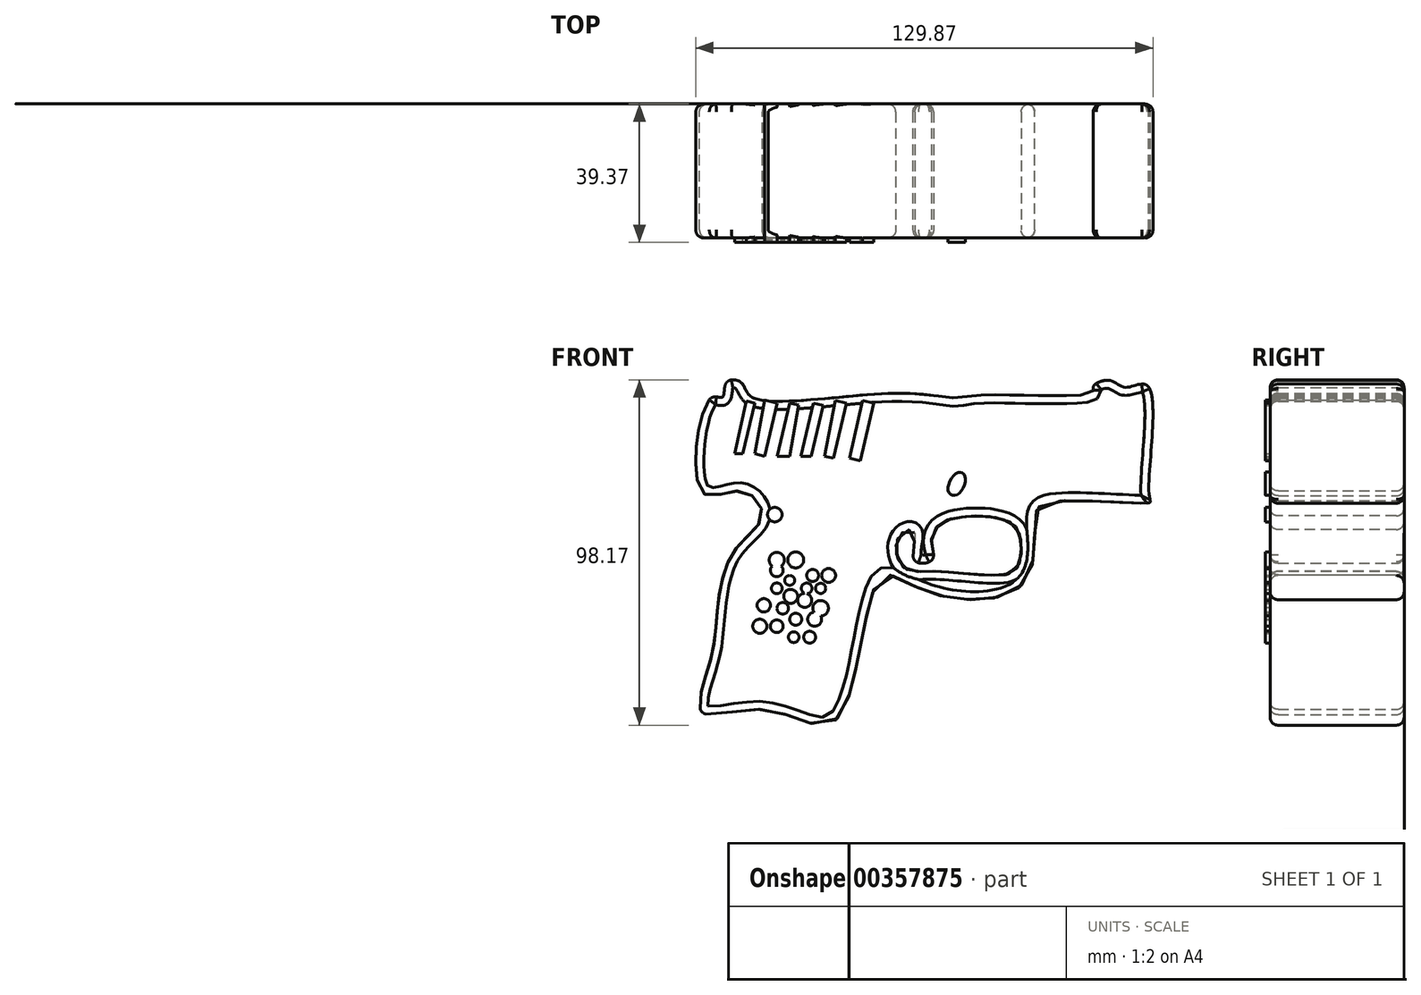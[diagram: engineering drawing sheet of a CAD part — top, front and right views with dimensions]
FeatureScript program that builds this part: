
annotation { "Feature Type Name" : "Feature", "Feature Type Description" : "" }
export const myFeature = defineFeature(function(context is Context, id is Id, definition is map)
    precondition{}
    {
        {
            var Q0;
            Q0=qCreatedBy(makeId("Front.planeOp"),FACE);
            var sketch = newSketch(context, id + "F0", { "sketchPlane" : qUnion([Q0])});
            skFitSpline(sketch, "E0", {"points": [v(-22.23, -45.44) * mm, v(-10, -5.42) * mm, v(2.22, -8.48) * mm, v(30.57, -7.09) * mm, v(34.18, 11.25) * mm, v(38.07, 16.35) * mm, v(66.7, 16.26) * mm, v(66.7, 18.2) * mm, v(66.42, 49.33) * mm, v(60.03, 49.05) * mm, v(55.58, 51) * mm, v(50.86, 49.33) * mm, v(50.58, 47.66) * mm, v(18.06, 46.83) * mm, v(11.95, 46) * mm, v(-5, 47.38) * mm, v(-46.13, 46.27) * mm, v(-49.19, 50.44) * mm, v(-53.36, 50.44) * mm, v(-54.47, 46.27) * mm, v(-57.8, 46) * mm, v(-60.3, 19.31) * mm, v(-49.19, 19.6) * mm, v(-43.2, 12.64) * mm, v(-51.13, 2.64) * mm, v(-56.14, -15.98) * mm, v(-58.08, -29.04) * mm, v(-60.33, -43.21) * mm, v(-41.96, -42.63) * mm, v(-22.23, -45.44) * mm]});
            skFitSpline(sketch, "E1", {"points": [v(-2.78, 8.2) * mm, v(-5.28, 3.75) * mm, v(-2.78, -2.36) * mm, v(4.45, -3.2) * mm, v(20.29, -4.3) * mm, v(28.9, -2.64) * mm, v(30.3, 4.86) * mm, v(27.23, 10.7) * mm, v(8.61, 10.98) * mm, v(4.9, 5.14) * mm, v(5, 0) * mm, v(0, 0) * mm, v(0, 7.92) * mm, v(-2.78, 8.2) * mm]});
            skSolve(sketch);
        }
        {
            var Q0;
            Q0=makeQuery(id+"F0.imprint","IMPRINT",FACE,{"disambiguationData":[TD([[makeQuery(id+"F0.imprint","IMPRINT",EDGE,{"derivedFrom":sQuery(id+"F0.wireOp",EDGE,"E0")}),1.0]])]});
            extrude(context, id + "F1", {"entities" : qUnion([Q0]), "depth" : 38.1 * mm});
        }
        {
            var Q0;
            Q0=makeQuery(id+"F1.opExtrude","CAP_FACE",FACE,{"disambiguationData":[OSD([sQuery(id+"F0.wireOp",EDGE,"E0"),sQuery(id+"F0.wireOp",EDGE,"E1")])],"isStart":false});
            var Q1;
            Q1=makeQuery(id+"F1.opExtrude","CAP_FACE",FACE,{"disambiguationData":[OSD([sQuery(id+"F0.wireOp",EDGE,"E0"),sQuery(id+"F0.wireOp",EDGE,"E1")])],"isStart":true});
            fillet(context, id + "F2", {"entities" : qUnion([Q0, Q1]), "radius" : 2.3 * mm, "tangentPropagation" : true, "allowEdgeOverflow" : false});
        }
        {
            var Q0;
            Q0=qCreatedBy(makeId("Front.planeOp"),FACE);
            var sketch = newSketch(context, id + "F3", { "sketchPlane" : qUnion([Q0])});
            skCircle(sketch, "E2", {"center": v(-29.74, -21.95) * mm, "radius": 1.7 * mm});
            skCircle(sketch, "E3", {"center": v(-34.27, -21.95) * mm, "radius": 1.53 * mm});
            skCircle(sketch, "E4", {"center": v(-39.08, -18.83) * mm, "radius": 1.81 * mm});
            skCircle(sketch, "E5", {"center": v(-43.9, -18.83) * mm, "radius": 2 * mm});
            skCircle(sketch, "E6", {"center": v(-42.77, -12.89) * mm, "radius": 1.9 * mm});
            skCircle(sketch, "E7", {"center": v(-28.32, -16.85) * mm, "radius": 1.98 * mm});
            skCircle(sketch, "E8", {"center": v(-33.7, -16.85) * mm, "radius": 1.7 * mm});
            skCircle(sketch, "E9", {"center": v(-37.39, -13.74) * mm, "radius": 1.65 * mm});
            skCircle(sketch, "E10", {"center": v(-39.08, -8.07) * mm, "radius": 1.53 * mm});
            skCircle(sketch, "E11", {"center": v(-35.12, -10.34) * mm, "radius": 1.98 * mm});
            skCircle(sketch, "E12", {"center": v(-31.15, -11.47) * mm, "radius": 2 * mm});
            skCircle(sketch, "E13", {"center": v(-26.62, -13.74) * mm, "radius": 2.21 * mm});
            skCircle(sketch, "E14", {"center": v(-24.36, -4.39) * mm, "radius": 1.98 * mm});
            skCircle(sketch, "E15", {"center": v(-26.62, -8.07) * mm, "radius": 1.44 * mm});
            skCircle(sketch, "E16", {"center": v(-30.59, -8.07) * mm, "radius": 1.53 * mm});
            skCircle(sketch, "E17", {"center": v(-35.4, -5.8) * mm, "radius": 1.42 * mm});
            skCircle(sketch, "E18", {"center": v(-39.08, -2.97) * mm, "radius": 1.8 * mm});
            skCircle(sketch, "E19", {"center": v(-39.08, 0) * mm, "radius": 2.16 * mm});
            skCircle(sketch, "E20", {"center": v(-33.7, 0) * mm, "radius": 2.27 * mm});
            skCircle(sketch, "E21", {"center": v(-28.89, -4.39) * mm, "radius": 1.7 * mm});
            skFitSpline(sketch, "E22", {"points": [v(12.18, 18.55) * mm, v(9.63, 19.68) * mm, v(12.18, 24.78) * mm, v(14.44, 23.65) * mm, v(12.18, 18.55) * mm]});
            skCircle(sketch, "E23", {"center": v(-39.65, 12.89) * mm, "radius": 2.06 * mm});
            skLineSegment(sketch, "E24", {"start": v(-50.98, 30.16) * mm, "end": v(-48.71, 30.16) * mm});
            skLineSegment(sketch, "E25", {"start": v(-48.71, 30.16) * mm, "end": v(-45.32, 44.6) * mm});
            skLineSegment(sketch, "E26", {"start": v(-45.32, 44.6) * mm, "end": v(-47.73, 45.18) * mm});
            skLineSegment(sketch, "E27", {"start": v(-47.73, 45.18) * mm, "end": v(-50.98, 30.16) * mm});
            skLineSegment(sketch, "E28", {"start": v(-45.32, 30.16) * mm, "end": v(-42.5, 29.5) * mm});
            skLineSegment(sketch, "E29", {"start": v(-42.5, 29.5) * mm, "end": v(-38.95, 44.6) * mm});
            skLineSegment(sketch, "E30", {"start": v(-38.95, 44.6) * mm, "end": v(-42.5, 45.44) * mm});
            skLineSegment(sketch, "E31", {"start": v(-42.5, 45.44) * mm, "end": v(-45.32, 30.16) * mm});
            skLineSegment(sketch, "E32", {"start": v(-38.95, 29.5) * mm, "end": v(-35.4, 44.6) * mm});
            skLineSegment(sketch, "E33", {"start": v(-35.4, 44.6) * mm, "end": v(-32.9, 44.02) * mm});
            skLineSegment(sketch, "E34", {"start": v(-32.9, 44.02) * mm, "end": v(-35.4, 29.5) * mm});
            skLineSegment(sketch, "E35", {"start": v(-35.4, 29.5) * mm, "end": v(-38.95, 29.5) * mm});
            skLineSegment(sketch, "E36", {"start": v(-32.29, 29.5) * mm, "end": v(-28.73, 44.6) * mm});
            skLineSegment(sketch, "E37", {"start": v(-28.73, 44.6) * mm, "end": v(-25.94, 43.95) * mm});
            skLineSegment(sketch, "E38", {"start": v(-25.94, 43.95) * mm, "end": v(-29.34, 29.5) * mm});
            skLineSegment(sketch, "E39", {"start": v(-29.34, 29.5) * mm, "end": v(-32.29, 29.5) * mm});
            skLineSegment(sketch, "E40", {"start": v(-25.49, 29.5) * mm, "end": v(-23.03, 28.92) * mm});
            skLineSegment(sketch, "E41", {"start": v(-23.03, 28.92) * mm, "end": v(-19.34, 44.6) * mm});
            skLineSegment(sketch, "E42", {"start": v(-19.34, 44.6) * mm, "end": v(-22.42, 45.33) * mm});
            skLineSegment(sketch, "E43", {"start": v(-22.42, 45.33) * mm, "end": v(-25.49, 29.5) * mm});
            skLineSegment(sketch, "E44", {"start": v(-18.4, 28.92) * mm, "end": v(-15.4, 28.22) * mm});
            skLineSegment(sketch, "E45", {"start": v(-15.4, 28.22) * mm, "end": v(-11.55, 44.6) * mm});
            skLineSegment(sketch, "E46", {"start": v(-11.55, 44.6) * mm, "end": v(-14.77, 45.37) * mm});
            skLineSegment(sketch, "E47", {"start": v(-14.77, 45.37) * mm, "end": v(-18.4, 28.92) * mm});
            skLineSegment(sketch, "E48", {"start": v(-42.5, 45.44) * mm, "end": v(-38.95, 44.6) * mm});
            skSolve(sketch);
        }
        {
            var Q0;
            Q0 = qSketchRegion(id + "F3", true);
            extrude(context, id + "F4", {"entities" : qUnion([Q0]), "operationType" : NewBodyOperationType.ADD, "depth" : 39.37 * mm});
        }
    });
